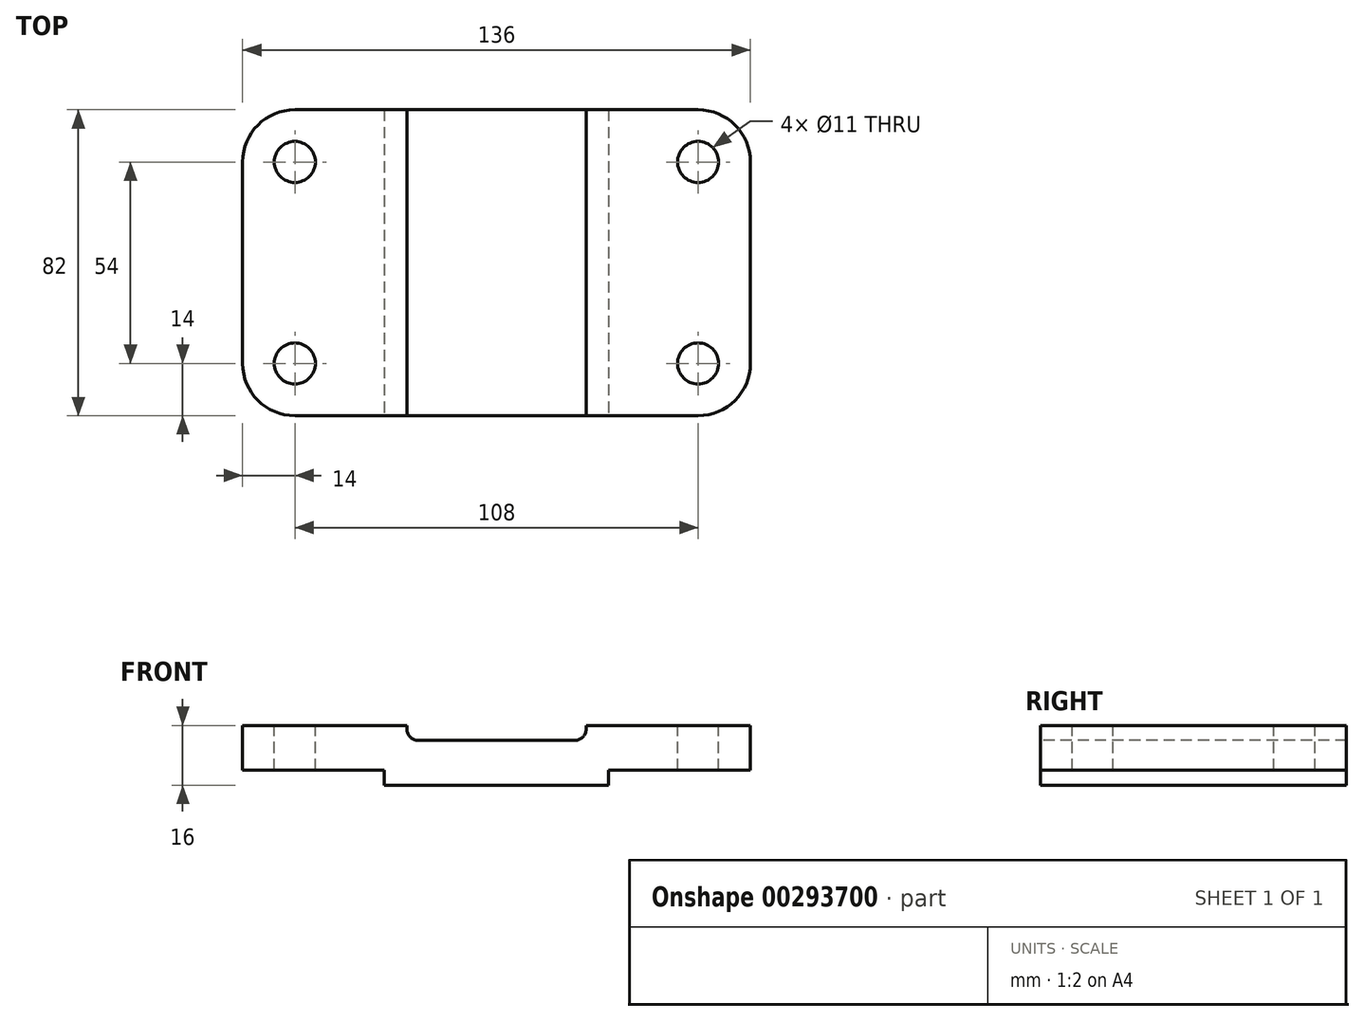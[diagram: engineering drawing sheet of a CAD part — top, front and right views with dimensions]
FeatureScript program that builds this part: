
annotation { "Feature Type Name" : "Feature", "Feature Type Description" : "" }
export const myFeature = defineFeature(function(context is Context, id is Id, definition is map)
    precondition{}
    {
        {
            var Q0;
            Q0=qCreatedBy(makeId("Front.planeOp"),FACE);
            var sketch = newSketch(context, id + "F0", { "sketchPlane" : qUnion([Q0])});
            skLineSegment(sketch, "E0", {"start": v(0, 0) * mm, "end": v(44, 0) * mm});
            skLineSegment(sketch, "E1", {"start": v(44, 0) * mm, "end": v(44, -1) * mm});
            skLineSegment(sketch, "E2", {"start": v(47, -4) * mm, "end": v(89, -4) * mm});
            skLineSegment(sketch, "E3", {"start": v(92, -1) * mm, "end": v(92, 0) * mm});
            skLineSegment(sketch, "E4", {"start": v(92, 0) * mm, "end": v(136, 0) * mm});
            skLineSegment(sketch, "E5", {"start": v(136, 0) * mm, "end": v(136, -12) * mm});
            skLineSegment(sketch, "E6", {"start": v(136, -12) * mm, "end": v(98, -12) * mm});
            skLineSegment(sketch, "E7", {"start": v(98, -12) * mm, "end": v(98, -16) * mm});
            skLineSegment(sketch, "E8", {"start": v(98, -16) * mm, "end": v(38, -16) * mm});
            skLineSegment(sketch, "E9", {"start": v(38, -16) * mm, "end": v(38, -12) * mm});
            skLineSegment(sketch, "E10", {"start": v(38, -12) * mm, "end": v(0, -12) * mm});
            skLineSegment(sketch, "E11", {"start": v(0, -12) * mm, "end": v(0, 0) * mm});
            skPoint(sketch, "E12.visualSharp", {"position": v(44, -4) * mm});
            skArc(sketch, "E12.filletArc", {"start": v(44, -1) * mm, "mid": v(44.88, -3.12) * mm, "end": v(47, -4) * mm});
            skPoint(sketch, "E13.visualSharp", {"position": v(92, -4) * mm});
            skArc(sketch, "E13.filletArc", {"start": v(89, -4) * mm, "mid": v(91.12, -3.12) * mm, "end": v(92, -1) * mm});
            skSolve(sketch);
        }
        {
            var Q0;
            Q0 = qSketchRegion(id + "F0", true);
            extrude(context, id + "F1", {"entities" : qUnion([Q0]), "oppositeDirection" : true, "depth" : 82 * mm});
        }
        {
            var Q0;
            Q0=makeQuery(id+"F1.opExtrude","CAP_EDGE",EDGE,{"disambiguationData":[OSD([sQuery(id+"F0.wireOp",EDGE,"E11")])],"isStart":false});
            fillet(context, id + "F2", {"entities" : qUnion([Q0]), "radius" : 14 * mm, "tangentPropagation" : true, "allowEdgeOverflow" : false});
        }
        {
            var Q0;
            Q0=makeQuery(id+"F1.opExtrude","CAP_EDGE",EDGE,{"disambiguationData":[OSD([sQuery(id+"F0.wireOp",EDGE,"E11")])],"isStart":true});
            fillet(context, id + "F3", {"entities" : qUnion([Q0]), "radius" : 14 * mm, "tangentPropagation" : true, "allowEdgeOverflow" : false});
        }
        {
            var Q0;
            Q0=makeQuery(id+"F1.opExtrude","CAP_EDGE",EDGE,{"disambiguationData":[OSD([sQuery(id+"F0.wireOp",EDGE,"E5")])],"isStart":true});
            var Q1;
            Q1=makeQuery(id+"F1.opExtrude","CAP_EDGE",EDGE,{"disambiguationData":[OSD([sQuery(id+"F0.wireOp",EDGE,"E5")])],"isStart":false});
            fillet(context, id + "F4", {"entities" : qUnion([Q0, Q1]), "radius" : 14 * mm, "tangentPropagation" : true, "allowEdgeOverflow" : false});
        }
        {
            var Q0;
            Q0=makeQuery(id+"F1.opExtrude","SWEPT_FACE",FACE,{"disambiguationData":[OSD([sQuery(id+"F0.wireOp",EDGE,"E0")])]});
            var sketch = newSketch(context, id + "F5", { "sketchPlane" : qUnion([Q0])});
            skLineSegment(sketch, "E14.0.0", {"start": v(0, 68) * mm, "end": v(0, 14) * mm});
            skArc(sketch, "E14.0.1", {"start": v(0, 14) * mm, "mid": v(4.1, 4.1) * mm, "end": v(14, 0) * mm});
            skLineSegment(sketch, "E14.0.2", {"start": v(14, 0) * mm, "end": v(44, 0) * mm});
            skLineSegment(sketch, "E14.0.3", {"start": v(44, 0) * mm, "end": v(44, 82) * mm});
            skLineSegment(sketch, "E14.0.4", {"start": v(44, 82) * mm, "end": v(14, 82) * mm});
            skArc(sketch, "E14.0.5", {"start": v(14, 82) * mm, "mid": v(4.1, 77.9) * mm, "end": v(0, 68) * mm});
            skCircle(sketch, "E15", {"center": v(14, 68) * mm, "radius": 5.5 * mm});
            skCircle(sketch, "E16.0.1.0", {"center": v(14, 14) * mm, "radius": 5.5 * mm});
            skCircle(sketch, "E16.1.0.0", {"center": v(122, 68) * mm, "radius": 5.5 * mm});
            skCircle(sketch, "E16.1.1.0", {"center": v(122, 14) * mm, "radius": 5.5 * mm});
            skLineSegment(sketch, "E16.direction1", {"start": v(14, 68) * mm, "end": v(122, 68) * mm, "construction": true});
            skLineSegment(sketch, "E16.direction2", {"start": v(14, 68) * mm, "end": v(14, 14) * mm, "construction": true});
            skSolve(sketch);
        }
        {
            var Q0;
            Q0=makeQuery(id+"F5.imprint","IMPRINT",FACE,{"disambiguationData":[TD([[makeQuery(id+"F5.imprint","IMPRINT",EDGE,{"derivedFrom":sQuery(id+"F5.wireOp",EDGE,"E15")}),1.0]])]});
            var Q1;
            Q1=makeQuery(id+"F5.imprint","IMPRINT",FACE,{"disambiguationData":[TD([[makeQuery(id+"F5.imprint","IMPRINT",EDGE,{"derivedFrom":sQuery(id+"F5.wireOp",EDGE,"E16.0.1.0")}),1.0]])]});
            var Q2;
            Q2=makeQuery(id+"F5.imprint","IMPRINT",FACE,{"disambiguationData":[TD([[makeQuery(id+"F5.imprint","IMPRINT",EDGE,{"derivedFrom":sQuery(id+"F5.wireOp",EDGE,"E16.1.1.0")}),1.0]])]});
            var Q3;
            Q3=makeQuery(id+"F5.imprint","IMPRINT",FACE,{"disambiguationData":[TD([[makeQuery(id+"F5.imprint","IMPRINT",EDGE,{"derivedFrom":sQuery(id+"F5.wireOp",EDGE,"E16.1.0.0")}),1.0]])]});
            extrude(context, id + "F6", {"entities" : qUnion([Q0, Q1, Q2, Q3]), "operationType" : NewBodyOperationType.REMOVE, "oppositeDirection" : true, "depth" : 10000 * mm});
        }
    });
